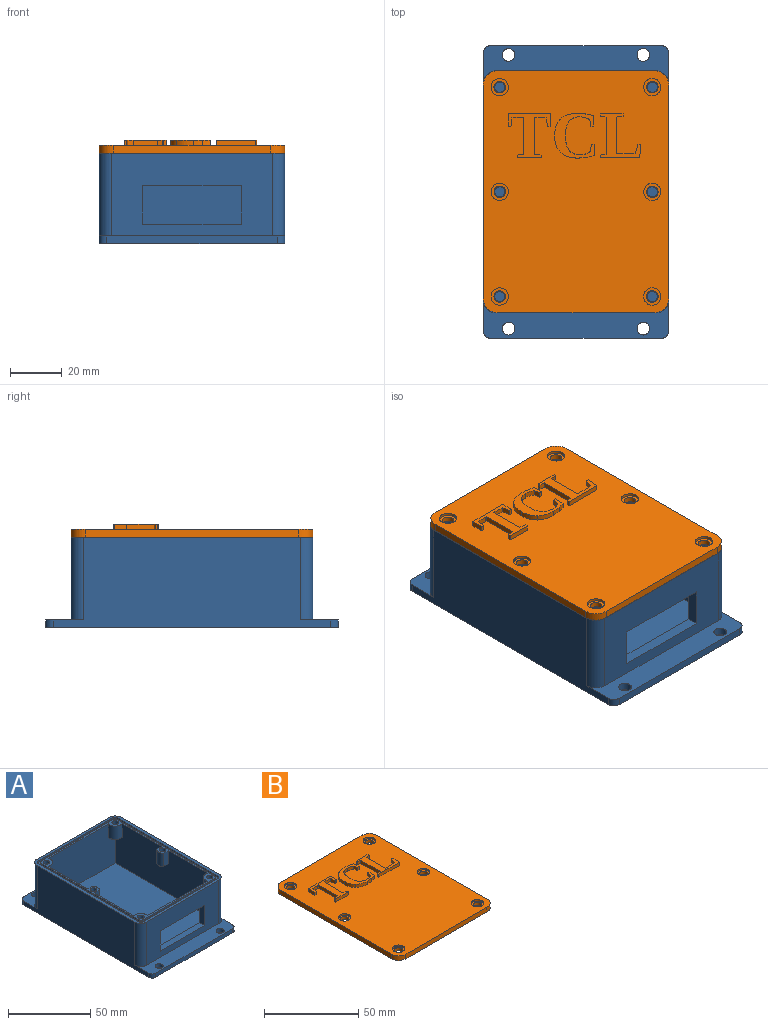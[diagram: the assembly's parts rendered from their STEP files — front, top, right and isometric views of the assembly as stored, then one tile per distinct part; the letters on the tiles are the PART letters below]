
ASSEMBLY  parts=2 mates=1
PART A: 115 faces, bbox 71.9x113.4x35 mm
  f0: plane 85x32mm, normal (1,0,0), area 2542.8mm2, adj f2,f3,f43,f44,f49,f51,f52,f54
  f1: plane 85x32mm, normal (-1,0,0), area 2542.8mm2, adj f2,f3,f43,f44,f55,f57,f58,f60
  f2: plane 63x32mm, normal (0,1,0), area 1327.9mm2, adj f0,f1,f43,f44,f45,f46,f47,f48
  f3: plane 63x32mm, normal (0,-1,0), area 1897.9mm2, adj f0,f1,f43,f44,f49,f51,f58,f60
  f4: plane 62.02x32mm, normal (0,-1,0), area 1414.5mm2, adj f5,f15,f16,f17,f45,f46,f47,f48
  f5: plane 93.67x71.86mm, normal (0,0,1), area 585.4mm2, adj f4,f8,f11,f15,f16,f18,f19,f20
  f6: plane 65.95x3mm, normal (0,-1,0), area 197.9mm2, adj f9,f10,f14,f17
  f7: plane 65.95x3mm, normal (0,1,0), area 197.9mm2, adj f12,f13,f14,f21
  f8: plane 107.45x35mm, normal (-1,0,0), area 3004.9mm2, adj f5,f9,f13,f14,f15,f17,f19,f21
  f9: cylinder r=2.95mm len=3mm, axis (0,0,-1), area 13.9mm2, adj f6,f8,f14,f17
  f10: cylinder r=2.95mm len=3mm, axis (0,0,-1), area 13.9mm2, adj f6,f11,f14,f17
  f11: plane 107.45x35mm, normal (1,0,0), area 3004.9mm2, adj f5,f10,f12,f14,f16,f17,f18,f21
  f12: cylinder r=2.95mm len=3mm, axis (0,0,-1), area 13.9mm2, adj f7,f11,f14,f21
  f13: cylinder r=2.95mm len=3mm, axis (0,0,-1), area 13.9mm2, adj f7,f8,f14,f21
  f14: plane 113.36x71.86mm, normal (0,0,-1), area 8062.3mm2, adj f6,f7,f8,f9,f10,f11,f12,f13
  f15: cylinder r=4.92mm len=32mm, axis (0,0,-1), area 247.4mm2, adj f4,f5,f8,f17
  f16: cylinder r=4.92mm len=32mm, axis (0,0,-1), area 247.4mm2, adj f4,f5,f11,f17
  f17: plane 71.86x14.77mm, normal (0,0,1), area 676mm2, adj f4,f6,f8,f9,f10,f11,f15,f16
  f18: cylinder r=4.92mm len=32mm, axis (0,0,-1), area 247.4mm2, adj f5,f11,f20,f21
  f19: cylinder r=4.92mm len=32mm, axis (0,0,-1), area 247.4mm2, adj f5,f8,f20,f21
  f20: plane 62.02x32mm, normal (0,1,0), area 1984.5mm2, adj f5,f18,f19,f21
  f21: plane 71.86x14.77mm, normal (0,0,1), area 676mm2, adj f7,f8,f11,f12,f13,f18,f19,f20
  f22: cylinder r=2.46mm len=4.92mm, axis (0,0,-1), area 46.4mm2, adj f14,f21
  f23: cylinder r=2.46mm len=4.92mm, axis (0,0,-1), area 46.4mm2, adj f14,f21
  f24: cylinder r=2.46mm len=4.92mm, axis (0,0,-1), area 46.4mm2, adj f14,f17
  f25: cylinder r=2.46mm len=4.92mm, axis (0,0,-1), area 46.4mm2, adj f14,f17
  f26: plane 86.29x1mm, normal (-1,0,0), area 86.3mm2, adj f5,f27,f41,f42
  f27: cylinder r=1.97mm len=1.97mm, axis (0,0,-1), area 3.1mm2, adj f5,f26,f28,f42
  f28: plane 63.98x1mm, normal (0,-1,0), area 64mm2, adj f5,f27,f29,f42
  f29: cylinder r=1.97mm len=1.97mm, axis (0,0,-1), area 3.1mm2, adj f5,f28,f30,f42
  f30: plane 86.29x1mm, normal (1,0,0), area 86.3mm2, adj f5,f29,f31,f42
  f31: cylinder r=1.97mm len=1.97mm, axis (0,0,-1), area 3.1mm2, adj f5,f30,f32,f42
  f32: plane 63.98x1mm, normal (0,1,0), area 64mm2, adj f5,f31,f41,f42
  f33: cylinder r=1.97mm len=1.97mm, axis (0,0,-1), area 3.1mm2, adj f34,f40,f42,f44
  f34: plane 83.34x1mm, normal (1,0,0), area 83.3mm2, adj f33,f35,f42,f44
  f35: cylinder r=1.97mm len=1.97mm, axis (0,0,-1), area 3.1mm2, adj f34,f36,f42,f44
  f36: plane 61.03x1mm, normal (0,-1,0), area 61mm2, adj f35,f37,f42,f44
  f37: cylinder r=1.97mm len=1.97mm, axis (0,0,-1), area 3.1mm2, adj f36,f38,f42,f44
  f38: plane 83.34x1mm, normal (-1,0,0), area 83.3mm2, adj f37,f39,f42,f44
  f39: cylinder r=1.97mm len=1.97mm, axis (0,0,-1), area 3.1mm2, adj f38,f40,f42,f44
  f40: plane 61.03x1mm, normal (0,1,0), area 61mm2, adj f33,f39,f42,f44
  f41: cylinder r=1.97mm len=1.97mm, axis (0,0,-1), area 3.1mm2, adj f5,f26,f32,f42
  f42: plane 90.23x67.92mm, normal (0,0,1), area 458.3mm2, adj f26,f27,f28,f29,f30,f31,f32,f33
  f43: plane 85x63mm, normal (0,0,1), area 5280.3mm2, adj f0,f1,f2,f3,f71,f72,f73,f74
  f44: plane 87.27x64.97mm, normal (0,0,1), area 420.7mm2, adj f0,f1,f2,f3,f33,f34,f35,f36
  f45: plane 15x4.34mm, normal (-1,0,0), area 65mm2, adj f2,f4,f46,f48
  f46: plane 38x4.34mm, normal (0,0,-1), area 164.8mm2, adj f2,f4,f45,f47
  f47: plane 15x4.34mm, normal (1,0,0), area 65mm2, adj f2,f4,f46,f48
  f48: plane 38x4.34mm, normal (0,0,1), area 164.8mm2, adj f2,f4,f45,f47
  f49: cylinder r=4.92mm len=10mm, axis (0,0,-1), area 99.7mm2, adj f0,f3,f44,f51
  f50: cylinder r=1.97mm len=10mm, axis (0,0,-1), area 123.7mm2, adj f44,f51
  f51: plane 6.03x6.03mm, normal (0,0,-1), area 18.9mm2, adj f0,f3,f49,f50
  f52: cylinder r=4.92mm len=10mm, axis (0,0,-1), area 99.7mm2, adj f0,f2,f44,f54
  f53: cylinder r=1.97mm len=10mm, axis (0,0,-1), area 123.7mm2, adj f44,f54
  f54: plane 6.03x6.03mm, normal (0,0,-1), area 18.9mm2, adj f0,f2,f52,f53
  f55: cylinder r=4.92mm len=10mm, axis (0,0,-1), area 99.7mm2, adj f1,f2,f44,f57
  f56: cylinder r=1.97mm len=10mm, axis (0,0,-1), area 123.7mm2, adj f44,f57
  f57: plane 6.03x6.03mm, normal (0,0,-1), area 18.9mm2, adj f1,f2,f55,f56
  f58: cylinder r=4.92mm len=10mm, axis (0,0,-1), area 99.8mm2, adj f1,f3,f44,f60
  f59: cylinder r=1.97mm len=10mm, axis (0,0,-1), area 123.7mm2, adj f44,f60
  f60: plane 6.04x6.03mm, normal (0,0,-1), area 19mm2, adj f1,f3,f58,f59
  f61: plane 10x3.94mm, normal (0,-1,0), area 39.4mm2, adj f1,f44,f63,f65
  f62: plane 10x3.94mm, normal (0,1,0), area 39.4mm2, adj f1,f44,f63,f65
  f63: cylinder r=3.94mm len=10mm, axis (0,0,-1), area 66.8mm2, adj f44,f61,f62,f65
  f64: cylinder r=1.97mm len=10mm, axis (0,0,-1), area 123.7mm2, adj f44,f65
  f65: plane 5.91x5.27mm, normal (0,0,-1), area 16.5mm2, adj f1,f61,f62,f63,f64
  f66: plane 10x3.94mm, normal (0,-1,0), area 39.4mm2, adj f0,f44,f67,f70
  f67: cylinder r=3.94mm len=10mm, axis (0,0,-1), area 66.8mm2, adj f44,f66,f69,f70
  f68: cylinder r=1.97mm len=10mm, axis (0,0,-1), area 123.7mm2, adj f44,f70
  f69: plane 10x3.94mm, normal (0,1,0), area 39.4mm2, adj f0,f44,f67,f70
  f70: plane 5.91x5.27mm, normal (0,0,-1), area 16.5mm2, adj f0,f66,f67,f68,f69
  f71: plane 4.08x2.07mm, normal (-0.89,0.45,0), area 9.1mm2, adj f43,f72,f79,f80
  f72: plane 4.08x2.05mm, normal (0.89,0.45,0), area 9.1mm2, adj f43,f71,f73,f80
  f73: plane 2.28x2mm, normal (0,1,0), area 4.6mm2, adj f43,f72,f74,f80
  f74: plane 6.12x3.29mm, normal (-0.88,-0.47,0), area 13.9mm2, adj f43,f73,f75,f80
  f75: plane 3.79x2mm, normal (-1,0,0), area 7.6mm2, adj f43,f74,f76,f80
  f76: plane 2.08x2mm, normal (0,-1,0), area 4.2mm2, adj f43,f75,f77,f80
  f77: plane 3.85x2mm, normal (1,0,0), area 7.7mm2, adj f43,f76,f78,f80
  f78: plane 6.05x3.29mm, normal (0.88,-0.48,0), area 13.8mm2, adj f43,f77,f79,f80
  f79: plane 2.26x2mm, normal (0,1,0), area 4.5mm2, adj f43,f71,f78,f80
  f80: plane 9.9x8.66mm, normal (0,0,1), area 32.2mm2, adj f71,f72,f73,f74,f75,f76,f77,f78
  f81: plane 5.76x2mm, normal (0,-1,0), area 11.5mm2, adj f43,f82,f84,f85
  f82: plane 2x0.95mm, normal (1,0,0), area 1.9mm2, adj f43,f81,f83,f85
  f83: plane 5.76x2mm, normal (0,1,0), area 11.5mm2, adj f43,f82,f84,f85
  f84: plane 2x0.95mm, normal (-1,0,0), area 1.9mm2, adj f43,f81,f83,f85
  f85: plane 5.76x0.95mm, normal (0,0,1), area 5.5mm2, adj f81,f82,f83,f84
  f86: extruded ~2.11x2mm, area 4.8mm2, adj f43,f87,f113,f114
  f87: extruded ~2x1.64mm, area 3.5mm2, adj f43,f86,f88,f114
  f88: extruded ~2x1.9mm, area 4.7mm2, adj f43,f87,f89,f114
  f89: extruded ~2x1.33mm, area 3mm2, adj f43,f88,f90,f114
  f90: extruded ~2x0.41mm, area 1.2mm2, adj f43,f89,f91,f114
  f91: extruded ~2x0.48mm, area 1mm2, adj f43,f90,f92,f114
  f92: extruded ~2x0.72mm, area 1.6mm2, adj f43,f91,f93,f114
  f93: extruded ~2x0.91mm, area 2mm2, adj f43,f92,f94,f114
  f94: extruded ~2x1.02mm, area 2.1mm2, adj f43,f93,f95,f114
  f95: extruded ~2x1.31mm, area 2.8mm2, adj f43,f94,f96,f114
  f96: plane 2x1.63mm, normal (0.92,-0.38,0), area 3.5mm2, adj f43,f95,f97,f114
  f97: extruded ~2x1.47mm, area 3.1mm2, adj f43,f96,f98,f114
  f98: extruded ~2x1.47mm, area 3mm2, adj f43,f97,f99,f114
  f99: extruded ~2.46x2mm, area 5.3mm2, adj f43,f98,f100,f114
  f100: extruded ~2.07x2mm, area 4.7mm2, adj f43,f99,f101,f114
  f101: extruded ~2x1.22mm, area 2.5mm2, adj f43,f100,f102,f114
  f102: extruded ~2x0.91mm, area 2.3mm2, adj f43,f101,f103,f114
  f103: extruded ~2x1.36mm, area 3.2mm2, adj f43,f102,f104,f114
  f104: extruded ~2x1.28mm, area 2.9mm2, adj f43,f103,f105,f114
  f105: extruded ~2x0.48mm, area 1.3mm2, adj f43,f104,f106,f114
  f106: extruded ~2x0.52mm, area 1.1mm2, adj f43,f105,f107,f114
  f107: extruded ~2x0.79mm, area 1.8mm2, adj f43,f106,f108,f114
  f108: extruded ~2x1.06mm, area 2.2mm2, adj f43,f107,f109,f114
  f109: extruded ~2x1.27mm, area 2.6mm2, adj f43,f108,f110,f114
  f110: extruded ~2x1.7mm, area 3.6mm2, adj f43,f109,f111,f114
  f111: plane 2x1.95mm, normal (-1,0,0), area 3.9mm2, adj f43,f110,f112,f114
  f112: extruded ~2.8x2mm, area 5.8mm2, adj f43,f111,f113,f114
  f113: extruded ~2.68x2mm, area 5.7mm2, adj f43,f86,f112,f114
  f114: plane 10.18x6.45mm, normal (0,0,1), area 37mm2, adj f86,f87,f88,f89,f90,f91,f92,f93
PART B: 84 faces, bbox 71.9x93.7x5 mm
  f0: cylinder r=2.23mm len=4.46mm, axis (0,0,-1), area 28mm2, adj f15,f27
  f1: cylinder r=2.23mm len=4.46mm, axis (0,0,-1), area 28mm2, adj f15,f25
  f2: cylinder r=2.23mm len=4.46mm, axis (0,0,-1), area 28mm2, adj f15,f23
  f3: cylinder r=2.23mm len=4.46mm, axis (0,0,-1), area 28mm2, adj f15,f21
  f4: cylinder r=2.23mm len=4.46mm, axis (0,0,-1), area 28mm2, adj f15,f19
  f5: cylinder r=2.23mm len=4.46mm, axis (0,0,-1), area 28mm2, adj f15,f17
  f6: plane 82.52x3mm, normal (1,0,0), area 247.6mm2, adj f7,f13,f14,f15
  f7: cylinder r=5.58mm len=5.58mm, axis (0,0,-1), area 26.3mm2, adj f6,f8,f14,f15
  f8: plane 60.71x3mm, normal (0,1,0), area 182.1mm2, adj f7,f9,f14,f15
  f9: cylinder r=5.58mm len=5.58mm, axis (0,0,-1), area 26.3mm2, adj f8,f10,f14,f15
  f10: plane 82.52x3mm, normal (-1,0,0), area 247.6mm2, adj f9,f11,f14,f15
  f11: cylinder r=5.58mm len=5.58mm, axis (0,0,-1), area 26.3mm2, adj f10,f12,f14,f15
  f12: plane 60.71x3mm, normal (0,-1,0), area 182.1mm2, adj f11,f13,f14,f15
  f13: cylinder r=5.58mm len=5.58mm, axis (0,0,-1), area 26.3mm2, adj f6,f12,f14,f15
  f14: plane 93.67x71.86mm, normal (0,0,1), area 6206mm2, adj f6,f7,f8,f9,f10,f11,f12,f13
  f15: plane 93.67x71.86mm, normal (0,0,-1), area 6610.7mm2, adj f0,f1,f2,f3,f4,f5,f6,f7
  f16: cylinder r=3.35mm len=6.69mm, axis (0,0,-1), area 21mm2, adj f14,f17
  f17: plane 6.69x6.69mm, normal (0,0,1), area 19.5mm2, adj f5,f16
  f18: cylinder r=3.35mm len=6.69mm, axis (0,0,-1), area 21mm2, adj f14,f19
  f19: plane 6.69x6.69mm, normal (0,0,1), area 19.5mm2, adj f4,f18
  f20: cylinder r=3.35mm len=6.69mm, axis (0,0,-1), area 21mm2, adj f14,f21
  f21: plane 6.69x6.69mm, normal (0,0,1), area 19.5mm2, adj f3,f20
  f22: cylinder r=3.35mm len=6.69mm, axis (0,0,-1), area 21mm2, adj f14,f23
  f23: plane 6.69x6.69mm, normal (0,0,1), area 19.5mm2, adj f2,f22
  f24: cylinder r=3.35mm len=6.69mm, axis (0,0,-1), area 21mm2, adj f14,f25
  f25: plane 6.69x6.69mm, normal (0,0,1), area 19.5mm2, adj f1,f24
  f26: cylinder r=3.35mm len=6.69mm, axis (0,0,-1), area 21mm2, adj f14,f27
  f27: plane 6.69x6.69mm, normal (0,0,1), area 19.5mm2, adj f0,f26
  f28: plane 2x0.92mm, normal (-1,0,0), area 1.8mm2, adj f14,f29,f45,f46
  f29: plane 9.33x2mm, normal (0,-1,0), area 18.7mm2, adj f14,f28,f30,f46
  f30: plane 2x0.92mm, normal (1,0,0), area 1.8mm2, adj f14,f29,f31,f46
  f31: plane 2.68x2mm, normal (0.13,0.99,0), area 5.4mm2, adj f14,f30,f32,f46
  f32: plane 14.24x2mm, normal (1,0,0), area 28.5mm2, adj f14,f31,f33,f46
  f33: plane 2x0.62mm, normal (0,-1,0), area 1.2mm2, adj f14,f32,f34,f46
  f34: extruded ~4.12x2mm, area 8.3mm2, adj f14,f33,f35,f46
  f35: plane 3.13x2mm, normal (-0.99,-0.11,0), area 6.3mm2, adj f14,f34,f36,f46
  f36: plane 2x1.16mm, normal (0,-1,0), area 2.3mm2, adj f14,f35,f37,f46
  f37: plane 4.71x2mm, normal (1,0,0), area 9.4mm2, adj f14,f36,f38,f46
  f38: plane 16.38x2mm, normal (0,1,0), area 32.8mm2, adj f14,f37,f39,f46
  f39: plane 4.71x2mm, normal (-1,0,0), area 9.4mm2, adj f14,f38,f40,f46
  f40: plane 2x1.14mm, normal (0,-1,0), area 2.3mm2, adj f14,f39,f41,f46
  f41: plane 3.13x2mm, normal (0.99,-0.11,0), area 6.3mm2, adj f14,f40,f42,f46
  f42: extruded ~4.05x2mm, area 8.1mm2, adj f14,f41,f43,f46
  f43: plane 2x0.64mm, normal (0,-1,0), area 1.3mm2, adj f14,f42,f44,f46
  f44: plane 14.26x2mm, normal (-1,0,0), area 28.5mm2, adj f14,f43,f45,f46
  f45: plane 2.67x2mm, normal (-0.13,0.99,0), area 5.4mm2, adj f14,f28,f44,f46
  f46: plane 16.85x16.38mm, normal (0,0,1), area 99mm2, adj f28,f29,f30,f31,f32,f33,f34,f35
  f47: extruded ~6.61x2.25mm, area 14.3mm2, adj f14,f48,f66,f67
  f48: extruded ~3.37x2mm, area 6.8mm2, adj f14,f47,f49,f67
  f49: extruded ~2.94x2mm, area 6.1mm2, adj f14,f48,f50,f67
  f50: plane 4.28x2mm, normal (1,-0.02,0), area 8.6mm2, adj f14,f49,f51,f67
  f51: plane 2x1.14mm, normal (0,1,0), area 2.3mm2, adj f14,f50,f52,f67
  f52: plane 2.77x2mm, normal (-0.99,0.14,0), area 5.6mm2, adj f14,f51,f53,f67
  f53: extruded ~2x1.67mm, area 3.8mm2, adj f14,f52,f54,f67
  f54: extruded ~2.48x2mm, area 5mm2, adj f14,f53,f55,f67
  f55: extruded ~4.1x2mm, area 9.3mm2, adj f14,f54,f56,f67
  f56: extruded ~5.38x2mm, area 11.3mm2, adj f14,f55,f57,f67
  f57: extruded ~5.64x2mm, area 11.8mm2, adj f14,f56,f58,f67
  f58: extruded ~4.26x2mm, area 9.6mm2, adj f14,f57,f59,f67
  f59: extruded ~3.86x2mm, area 8.2mm2, adj f14,f58,f60,f67
  f60: plane 2.44x2mm, normal (-0.99,-0.14,0), area 4.9mm2, adj f14,f59,f61,f67
  f61: plane 2x1.13mm, normal (0,-1,0), area 2.3mm2, adj f14,f60,f62,f67
  f62: plane 4.05x2mm, normal (1,0.02,0), area 8.1mm2, adj f14,f61,f63,f67
  f63: extruded ~6.07x2mm, area 12.3mm2, adj f14,f62,f64,f67
  f64: extruded ~6.7x2.24mm, area 14.5mm2, adj f14,f63,f65,f67
  f65: extruded ~6.57x2.27mm, area 14.3mm2, adj f14,f64,f66,f67
  f66: extruded ~6.24x2.37mm, area 13.7mm2, adj f14,f47,f65,f67
  f67: plane 17.3x15.37mm, normal (0,0,1), area 96.3mm2, adj f47,f48,f49,f50,f51,f52,f53,f54
  f68: plane 2.6x2mm, normal (0.13,-0.99,0), area 5.2mm2, adj f14,f69,f82,f83
  f69: plane 2x0.92mm, normal (1,0,0), area 1.8mm2, adj f14,f68,f70,f83
  f70: plane 8.71x2mm, normal (0,1,0), area 17.4mm2, adj f14,f69,f71,f83
  f71: plane 2x0.92mm, normal (-1,0,0), area 1.8mm2, adj f14,f70,f72,f83
  f72: plane 2.15x2mm, normal (-0.15,-0.99,0), area 4.3mm2, adj f14,f71,f73,f83
  f73: plane 14.35x2mm, normal (-1,0,0), area 28.7mm2, adj f14,f72,f74,f83
  f74: plane 2.16x2mm, normal (-0.16,0.99,0), area 4.4mm2, adj f14,f73,f75,f83
  f75: plane 2x0.92mm, normal (-1,0,0), area 1.8mm2, adj f14,f74,f76,f83
  f76: plane 15.17x2mm, normal (0,-1,0), area 30.3mm2, adj f14,f75,f77,f83
  f77: plane 5.09x2mm, normal (1,-0.09,0), area 10.2mm2, adj f14,f76,f78,f83
  f78: plane 2x1.13mm, normal (0,1,0), area 2.3mm2, adj f14,f77,f79,f83
  f79: plane 3.51x2mm, normal (-0.96,0.28,0), area 7.3mm2, adj f14,f78,f80,f83
  f80: extruded ~3.94x2mm, area 7.9mm2, adj f14,f79,f81,f83
  f81: plane 3.43x2mm, normal (0,1,0), area 6.9mm2, adj f14,f80,f82,f83
  f82: plane 14.28x2mm, normal (1,0,0), area 28.6mm2, adj f14,f68,f81,f83
  f83: plane 16.85x15.65mm, normal (0,0,1), area 92.2mm2, adj f68,f69,f70,f71,f72,f73,f74,f75
PLACE A t=(11.01,29.11,-14.51)mm
PLACE B t=(11.02,29.11,20.49)mm
MATE fastened B.f3 <-> A.f53  axis (0,0,-1) through (-18.51,-11.41,20.49)mm
